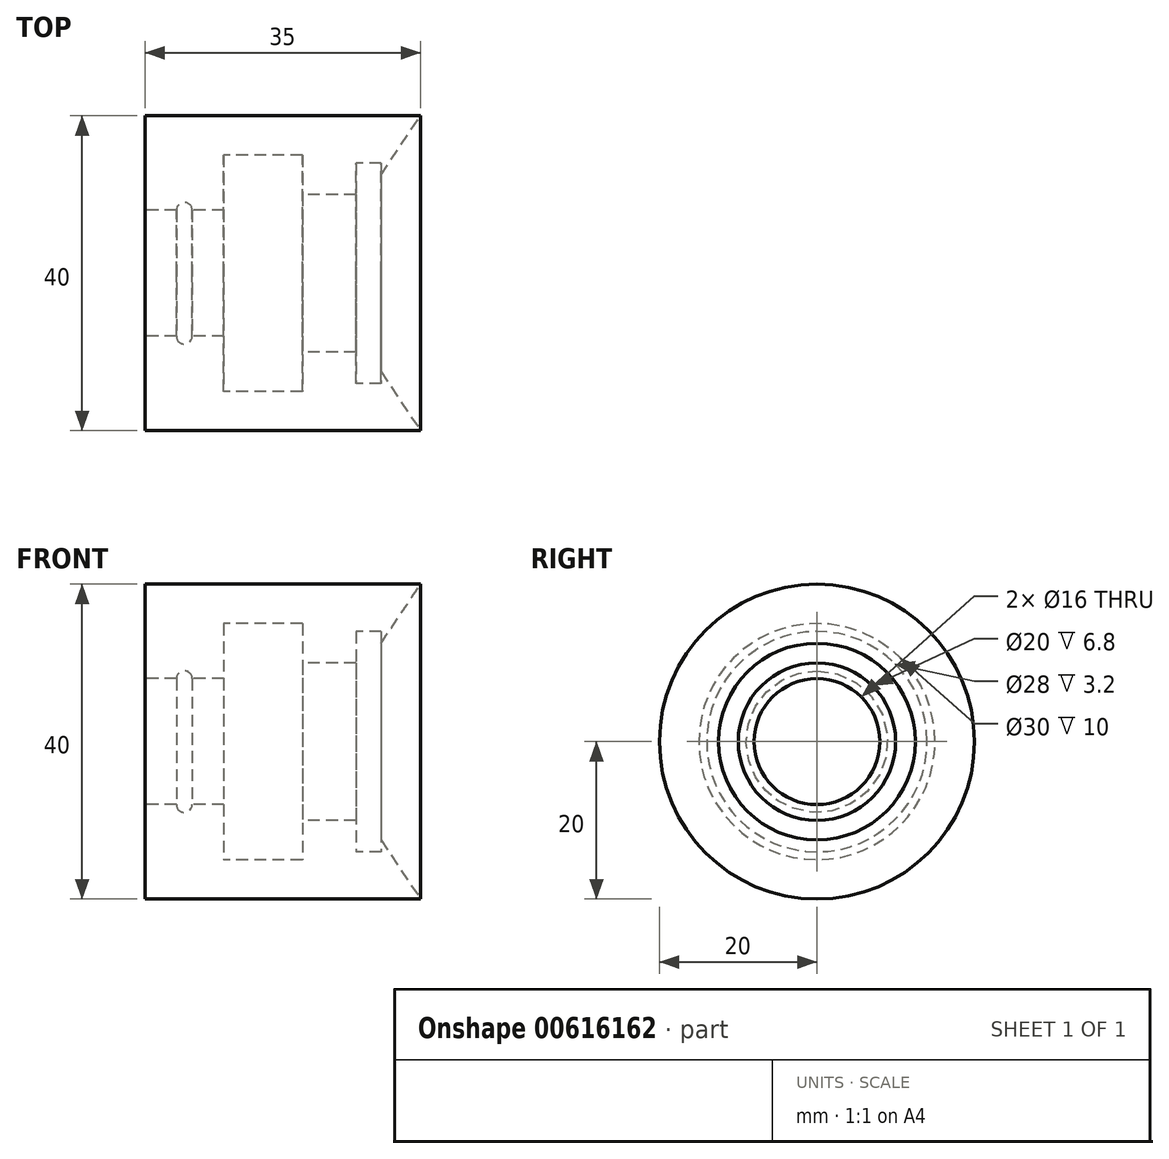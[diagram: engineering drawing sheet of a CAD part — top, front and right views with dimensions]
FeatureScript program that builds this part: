
annotation { "Feature Type Name" : "Feature", "Feature Type Description" : "" }
export const myFeature = defineFeature(function(context is Context, id is Id, definition is map)
    precondition{}
    {
        {
            var Q0;
            Q0=qCreatedBy(makeId("Front.planeOp"),FACE);
            var sketch = newSketch(context, id + "F0", { "sketchPlane" : qUnion([Q0])});
            skLineSegment(sketch, "E0", {"start": v(3.2, 8) * mm, "end": v(3.2, 20) * mm});
            skLineSegment(sketch, "E1", {"start": v(3.2, 20) * mm, "end": v(38.2, 20) * mm});
            skLineSegment(sketch, "E2.0", {"start": v(3.2, 8) * mm, "end": v(7.2, 8) * mm});
            skLineSegment(sketch, "E3.0", {"start": v(13.2, 15) * mm, "end": v(23.2, 15) * mm});
            skLineSegment(sketch, "E4", {"start": v(13.2, 8) * mm, "end": v(13.2, 15) * mm});
            skLineSegment(sketch, "E5", {"start": v(23.2, 15) * mm, "end": v(23.2, 10) * mm});
            skLineSegment(sketch, "E6.0", {"start": v(23.2, 10) * mm, "end": v(30, 10) * mm});
            skLineSegment(sketch, "E7", {"start": v(30, 10) * mm, "end": v(30, 14) * mm});
            skLineSegment(sketch, "E8", {"start": v(30, 14) * mm, "end": v(33.2, 14) * mm});
            skLineSegment(sketch, "E9", {"start": v(33.2, 14) * mm, "end": v(33.2, 12.5) * mm});
            skLineSegment(sketch, "E10", {"start": v(33.2, 12.5) * mm, "end": v(38.2, 20) * mm});
            skLineSegment(sketch, "E11", {"start": v(59.35, 0) * mm, "end": v(-7.25, 0) * mm, "construction": true});
            skArc(sketch, "E12", {"start": v(9.2, 8) * mm, "mid": v(8.2, 9) * mm, "end": v(7.2, 8) * mm});
            skLineSegment(sketch, "E13.trimOffspring", {"start": v(9.2, 8) * mm, "end": v(13.2, 8) * mm});
            skSolve(sketch);
        }
        {
            var Q0;
            Q0 = qSketchRegion(id + "F0", true);
            var Q1;
            Q1=sQuery(id+"F0.wireOp",EDGE,"E11");
            revolve(context, id + "F1", {"entities" : qUnion([Q0]), "axis" : qUnion([Q1]), "revolveType" : RevolveType.FULL, "oppositeDirection" : true});
        }
    });
